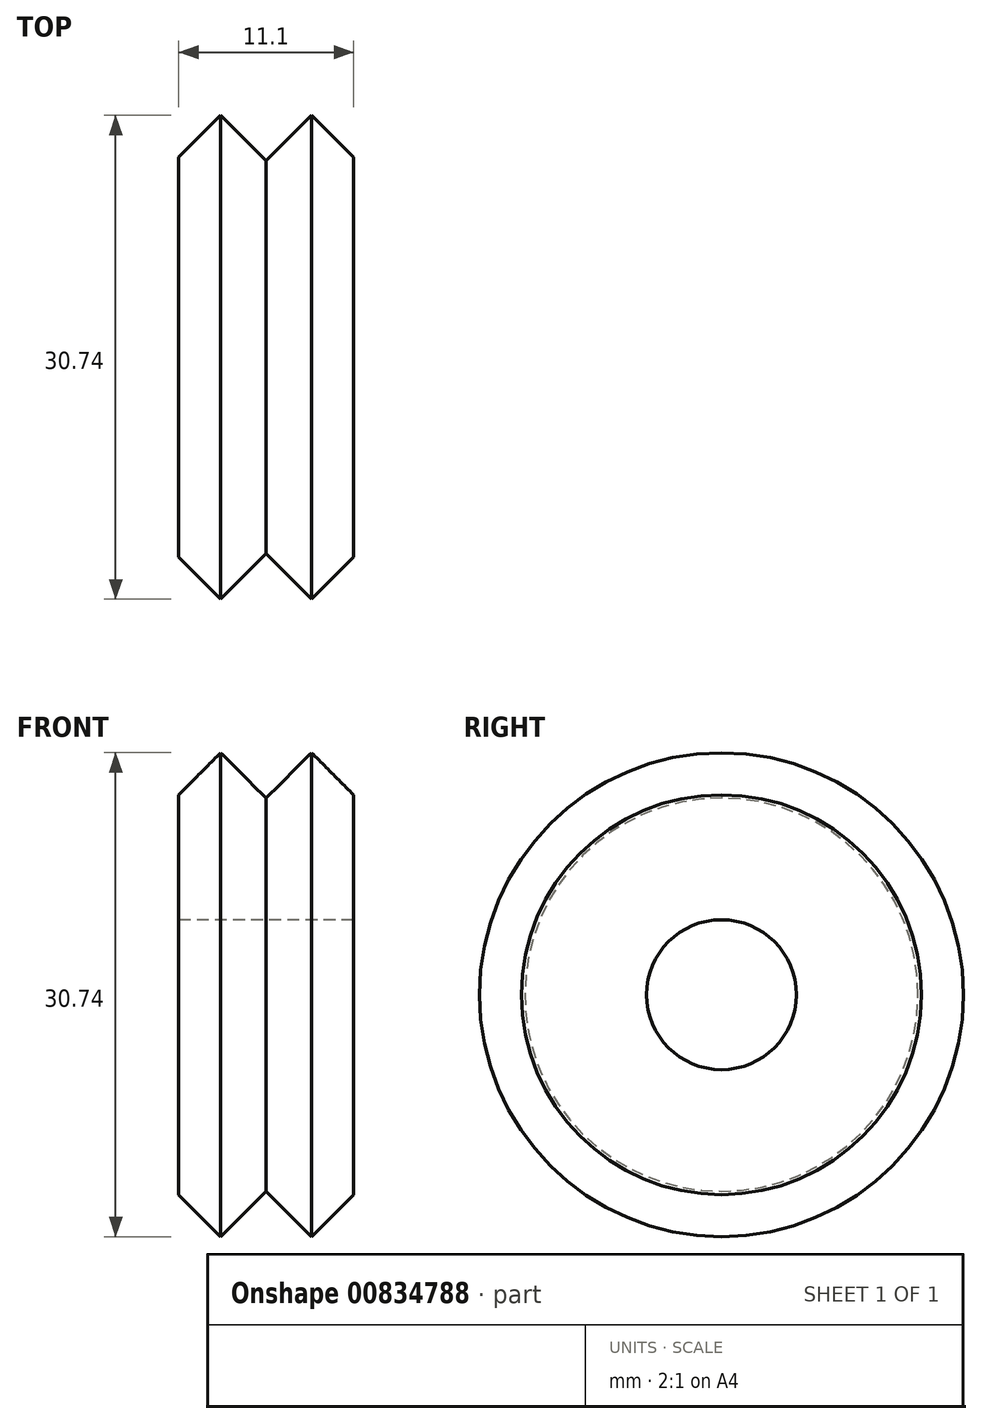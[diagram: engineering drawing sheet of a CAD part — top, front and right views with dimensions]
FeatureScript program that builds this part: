
annotation { "Feature Type Name" : "Feature", "Feature Type Description" : "" }
export const myFeature = defineFeature(function(context is Context, id is Id, definition is map)
    precondition{}
    {
        {
            var Q0;
            Q0=qCreatedBy(makeId("Top.planeOp"),FACE);
            var sketch = newSketch(context, id + "F0", { "sketchPlane" : qUnion([Q0])});
            skLineSegment(sketch, "E0", {"start": v(-8.16, 0) * mm, "end": v(9.09, 0) * mm, "construction": true});
            skLineSegment(sketch, "E1", {"start": v(-5.55, 4.76) * mm, "end": v(5.55, 4.76) * mm});
            skLineSegment(sketch, "E2", {"start": v(5.55, 4.76) * mm, "end": v(5.55, 12.7) * mm});
            skLineSegment(sketch, "E3", {"start": v(5.55, 12.7) * mm, "end": v(2.88, 15.37) * mm});
            skLineSegment(sketch, "E4", {"start": v(-2.88, 15.37) * mm, "end": v(-5.55, 12.7) * mm});
            skLineSegment(sketch, "E5", {"start": v(-5.55, 12.7) * mm, "end": v(-5.55, 4.76) * mm});
            skLineSegment(sketch, "E6", {"start": v(0, 0) * mm, "end": v(0, 12.67) * mm, "construction": true});
            skPoint(sketch, "E7.center.orphan", {"position": v(0, 12.67) * mm});
            skLineSegment(sketch, "E8", {"start": v(-2.88, 15.37) * mm, "end": v(0, 12.48) * mm});
            skLineSegment(sketch, "E9", {"start": v(0, 12.48) * mm, "end": v(2.88, 15.37) * mm});
            skSolve(sketch);
        }
        {
            var Q0;
            Q0 = qSketchRegion(id + "F0", true);
            var Q1;
            Q1=sQuery(id+"F0.wireOp",EDGE,"E0");
            revolve(context, id + "F1", {"surfaceOperationType" : NewSurfaceOperationType.NEW, "entities" : qUnion([Q0]), "axis" : qUnion([Q1]), "revolveType" : RevolveType.FULL});
        }
    });
